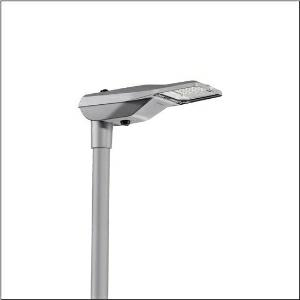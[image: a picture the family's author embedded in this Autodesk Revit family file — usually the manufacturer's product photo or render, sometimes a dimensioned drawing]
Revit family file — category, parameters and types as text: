
# Revit family: streetlight_sl_21_iq_micro___st1_0a_5xe1d31y08cb_1c09
name_source: partatom
category: Lighting Fixtures
units: mm (PartAtom-declared; Revit-internal decimal feet)

## family parameters
Cut with Voids When Loaded = No
Host = Face
Light Source = No
Part Type = Normal
Room Calculation Point = No
Round Connector Dimension = Use Diameter
Shared = No

## types (1)
- --- (1 x LED, 2880 lm, 19.1 W, 3000K)
    Apparent Load = 19 VA
    CIE Flux Codes = 37 72 97 100 100
    Color Rendering = 70
    Color Temperature = 3000K
    Default Elevation = 1800 mm
    Description = Streetlight SL 21 iQ micro, mast luminaire, primary light control with lens, of PMMA, primary optical cover: cover, of toughened safety glass, transparent, light distribution: ST1.0a, light emission: direct distribution, primary light characteristic: asymmetric, installation type: post-top, side-entry, LED, High Power LED, rated luminous flux: 2.880lm, luminous efficacy: 151lm/W, light colour: 730, colour temperature: 3000K, control gear: iQ-Street Remote, D4i with power reduction, control: pre-setting: logarithmic dimming characteristic, Street-Remote, Auto-Match, Temp-Guard, Lumen-Switch, Night-Set, Smart-Wire, Light-Fading, Desk-Remote (wireless, voltage-free reading and setting of iQ features in the workshop via application-optimized NFC function/RFID function), optimised constant luminous flux control (CLO 2.0), mains connection: 220..240V, AC, 50/60Hz, start of lifetime: 19W, end of service life: 20W, reduction: 9W, luminaire housing, of diecast aluminium, powder-coated, Siteco® metallic grey (DB 702S), corrosivity category C5 mid according to DIN EN ISO 12944, please order mast flange separately, inclination adjustable: 0°, 5°, 10°, 15°, sealing non-destructively replaceable, multi-level sealing system, length: 528mm, width: 235mm, height: 110mm, mast flange for spigot size: 42mm (side-entry): 5XC10008XM4, 60/48mm (side-entry/post-top): 5XC10108XM2, 76/60mm (side-entry/post-top): 5XC10108XM1, mounting height: 4..8m, Smart Interface below and above, protection rating (complete): IP66, insulation class (complete): insulation class II (safety insulation), certification: CE, ENEC, ENEC+, VDE, impact resistance: IK10, permissible operating ambient temperature for outdoor applications: -40..+50°C, standard-compliant lighting for roads and squares, packaging unit: 1 piece

Light Distribution: ST1.0a
    Height = 110 mm
    Lamp = 1 x LED
    Lamp Light Flux = 2880 lm
    Lamp Power = 19.1 W
    Lamp count = 1
    Length = 528 mm
    Luminous efficacy = 151 lm/W
    Manufacturer = Siteco
    ModVariant = No
    Model = 5XE1D31Y08CB
    Number of Poles = 1
    OnlyDefault = Yes
    Power Factor = 1
    Product Name = Streetlight SL 21 iQ micro | ST1.0a
    Product group = mast luminaire | pylon top
    ProductGroupID = 6100
    Protection Class = Protection class II
    Protection Degree = IP 66
    RLX_Detail_Level = 1
    RLX_Emergency_Light_Flux = 0 lm
    RLX_Emergency_Type = 0
    RLX_Emergency_Type_DB = No
    RlxData = <blob elided: 98473 chars, md5=8fb7a7ce>
    Socket = socket
    Standby Power = 0 W
    System Light Flux = 2880 lm
    System Power = 19 W
    Type Comments = factory setting: luminous flux: 100 % | dim-lin: 254 | 387 mA
    Type Image = l_1007239.jpg
    URL = http://relux.com
    VarID = @adj_115456
    Voltage = 0 V
    Weight = 0.00 kg
    Width = 235 mm

## geometry (parser evidence)
native form markers: Blend x4, Sweep x10
no freeform markers — native parametric forms only
